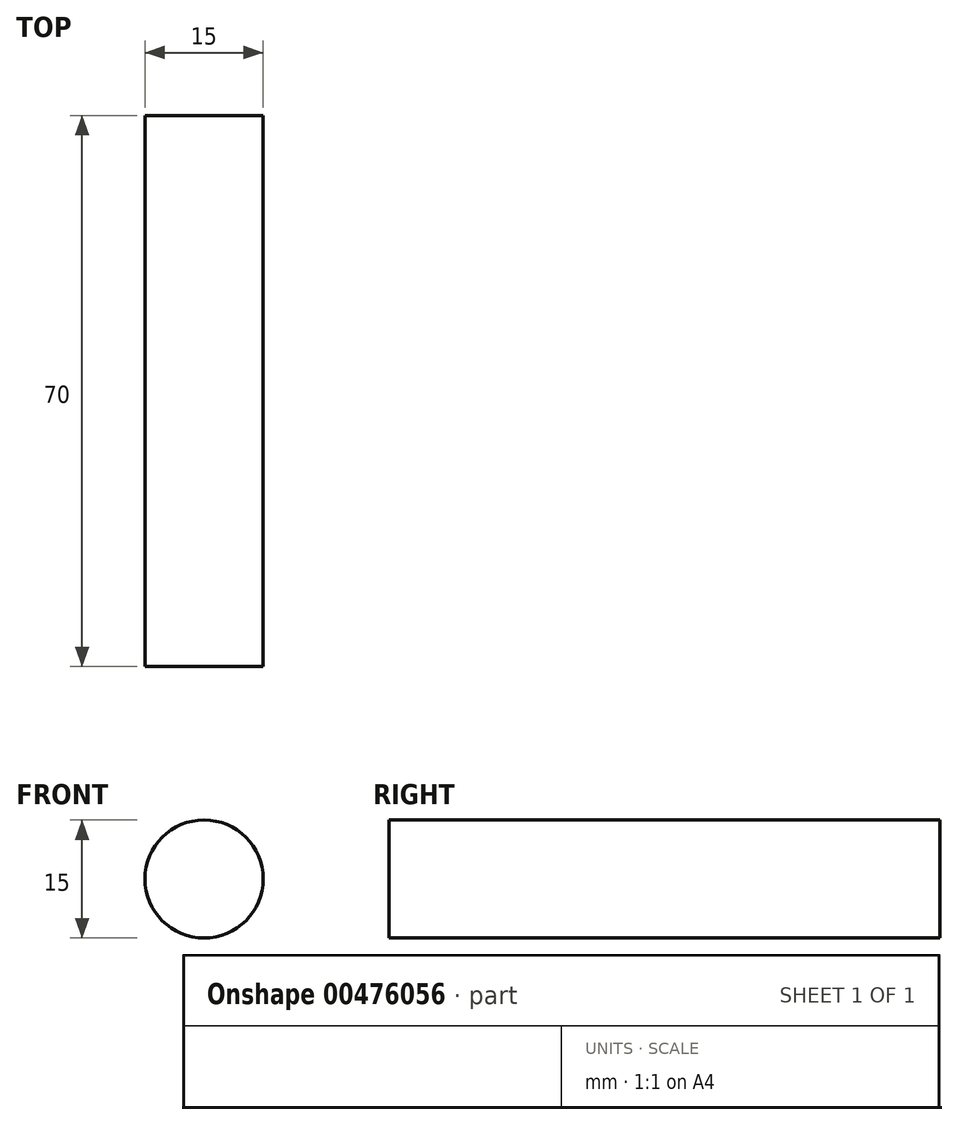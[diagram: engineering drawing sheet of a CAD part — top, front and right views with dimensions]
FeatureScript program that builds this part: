
annotation { "Feature Type Name" : "Feature", "Feature Type Description" : "" }
export const myFeature = defineFeature(function(context is Context, id is Id, definition is map)
    precondition{}
    {
        {
            var Q0;
            Q0=qCreatedBy(makeId("Front.planeOp"),FACE);
            var sketch = newSketch(context, id + "F0", { "sketchPlane" : qUnion([Q0])});
            skCircle(sketch, "E0", {"center": v(0, 0) * mm, "radius": 7.5 * mm});
            skSolve(sketch);
        }
        {
            var Q0;
            Q0 = qSketchRegion(id + "F0", true);
            extrude(context, id + "F1", {"entities" : qUnion([Q0]), "endBound" : BoundingType.SYMMETRIC, "depth" : 70 * mm});
        }
    });
